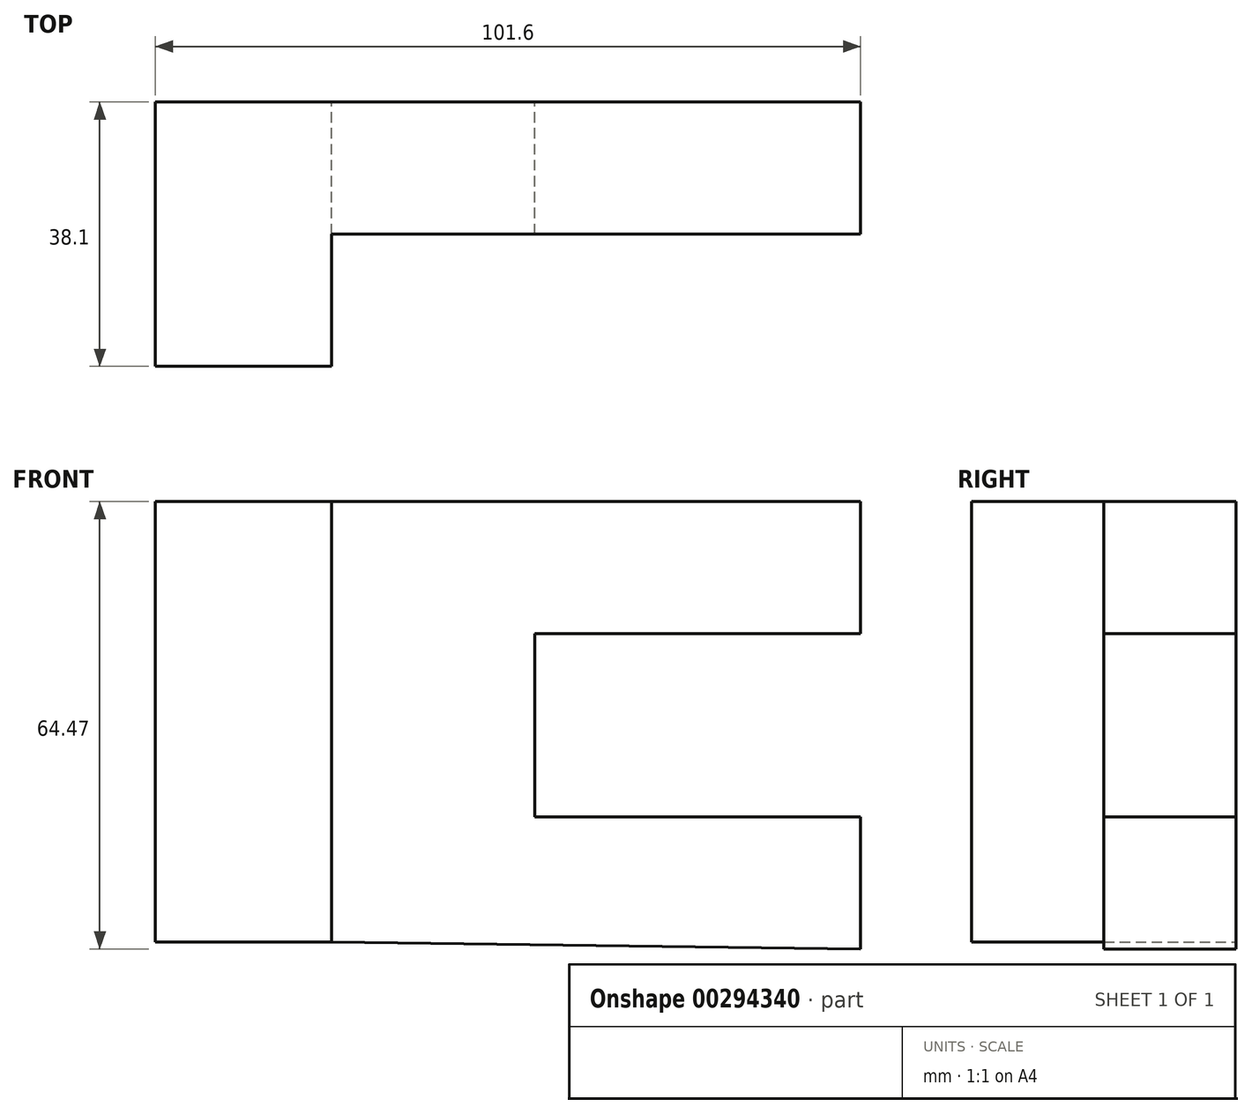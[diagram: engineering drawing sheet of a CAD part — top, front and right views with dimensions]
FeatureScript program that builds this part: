
annotation { "Feature Type Name" : "Feature", "Feature Type Description" : "" }
export const myFeature = defineFeature(function(context is Context, id is Id, definition is map)
    precondition{}
    {
        {
            var Q0;
            Q0=qCreatedBy(makeId("Front.planeOp"),FACE);
            var sketch = newSketch(context, id + "F0", { "sketchPlane" : qUnion([Q0])});
            skLineSegment(sketch, "E0.bottom", {"start": v(-62.42, 45.42) * mm, "end": v(-37.02, 45.42) * mm});
            skLineSegment(sketch, "E0.top", {"start": v(-62.42, -18.08) * mm, "end": v(-37.02, -18.08) * mm});
            skLineSegment(sketch, "E0.left", {"start": v(-62.42, 45.42) * mm, "end": v(-62.42, -18.08) * mm});
            skLineSegment(sketch, "E0.right", {"start": v(-37.02, 45.42) * mm, "end": v(-37.02, -18.08) * mm});
            skLineSegment(sketch, "E1", {"start": v(-37.02, 45.42) * mm, "end": v(39.18, 45.42) * mm});
            skLineSegment(sketch, "E2", {"start": v(39.18, 45.42) * mm, "end": v(39.18, 26.37) * mm});
            skLineSegment(sketch, "E3", {"start": v(39.18, 26.37) * mm, "end": v(-7.75, 26.37) * mm});
            skLineSegment(sketch, "E4", {"start": v(-7.75, 26.37) * mm, "end": v(-7.75, 0) * mm});
            skLineSegment(sketch, "E5", {"start": v(-7.75, 0) * mm, "end": v(39.18, 0) * mm});
            skLineSegment(sketch, "E6", {"start": v(39.18, 0) * mm, "end": v(39.18, -19.05) * mm});
            skLineSegment(sketch, "E7", {"start": v(39.18, -19.05) * mm, "end": v(-37.02, -18.08) * mm});
            skSolve(sketch);
        }
        {
            var Q0;
            Q0 = qSketchRegion(id + "F0", true);
            extrude(context, id + "F1", {"entities" : qUnion([Q0]), "depth" : 19.05 * mm});
        }
        {
            var Q0;
            Q0=makeQuery(id+"F1.opExtrude","CAP_FACE",FACE,{"disambiguationData":[OSD([sQuery(id+"F0.wireOp",EDGE,"E0.bottom"),sQuery(id+"F0.wireOp",EDGE,"E0.top"),sQuery(id+"F0.wireOp",EDGE,"E0.left"),sQuery(id+"F0.wireOp",EDGE,"E1"),sQuery(id+"F0.wireOp",EDGE,"E2"),sQuery(id+"F0.wireOp",EDGE,"E3"),sQuery(id+"F0.wireOp",EDGE,"E4"),sQuery(id+"F0.wireOp",EDGE,"E5"),sQuery(id+"F0.wireOp",EDGE,"E6"),sQuery(id+"F0.wireOp",EDGE,"E7")])],"isStart":false});
            var sketch = newSketch(context, id + "F2", { "sketchPlane" : qUnion([Q0])});
            skLineSegment(sketch, "E8.bottom", {"start": v(-62.42, 45.42) * mm, "end": v(-37.02, 45.42) * mm});
            skLineSegment(sketch, "E8.top", {"start": v(-62.42, -18.08) * mm, "end": v(-37.02, -18.08) * mm});
            skLineSegment(sketch, "E8.left", {"start": v(-62.42, 45.42) * mm, "end": v(-62.42, -18.08) * mm});
            skLineSegment(sketch, "E8.right", {"start": v(-37.02, 45.42) * mm, "end": v(-37.02, -18.08) * mm});
            skSolve(sketch);
        }
        {
            var Q0;
            Q0 = qSketchRegion(id + "F2", true);
            extrude(context, id + "F3", {"entities" : qUnion([Q0]), "operationType" : NewBodyOperationType.ADD, "depth" : 19.05 * mm});
        }
    });
